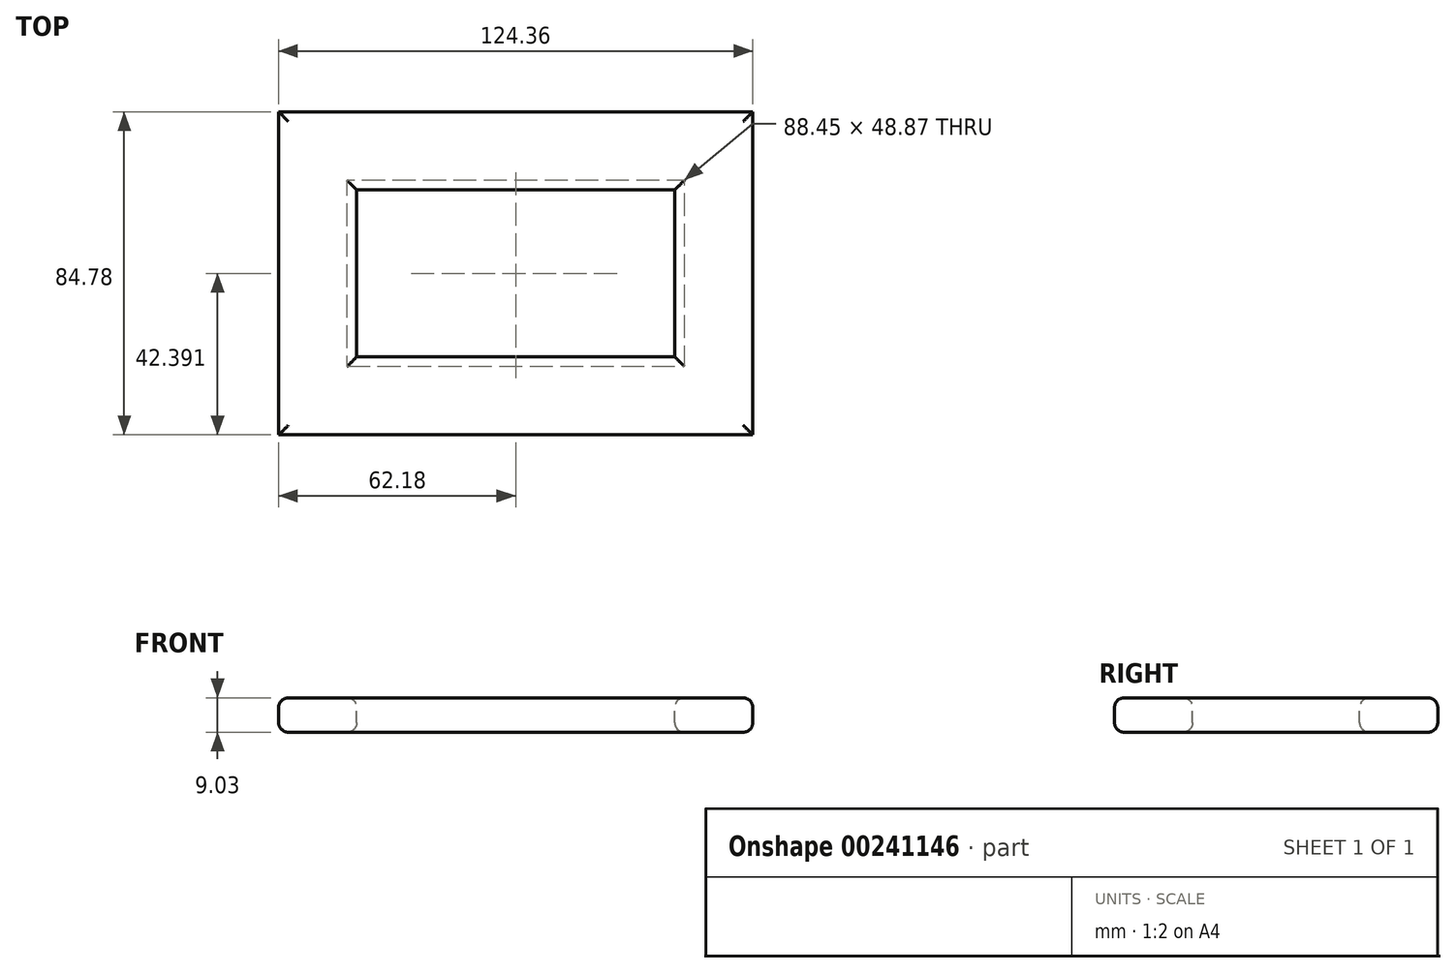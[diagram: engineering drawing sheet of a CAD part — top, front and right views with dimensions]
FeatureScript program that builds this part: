
annotation { "Feature Type Name" : "Feature", "Feature Type Description" : "" }
export const myFeature = defineFeature(function(context is Context, id is Id, definition is map)
    precondition{}
    {
        {
            var Q0;
            Q0=qCreatedBy(makeId("Top.planeOp"),FACE);
            var sketch = newSketch(context, id + "F0", { "sketchPlane" : qUnion([Q0])});
            skLineSegment(sketch, "E0.bottom", {"start": v(-49.05, 27.56) * mm, "end": v(54.15, 27.56) * mm});
            skLineSegment(sketch, "E0.top", {"start": v(-49.05, -36.06) * mm, "end": v(54.15, -36.06) * mm});
            skLineSegment(sketch, "E0.left", {"start": v(-49.05, 27.56) * mm, "end": v(-49.05, -36.06) * mm});
            skLineSegment(sketch, "E0.right", {"start": v(54.15, 27.56) * mm, "end": v(54.15, -36.06) * mm});
            skSolve(sketch);
        }
        {
            var Q0;
            Q0=sQuery(id+"F0.wireOp",VERTEX,"E0.left.end");
            var Q1;
            Q1=sQuery(id+"F0.wireOp",EDGE,"E0.left");
            cPlane(context, id + "F1", {"entities" : qUnion([Q0, Q1]), "cplaneType" : CPlaneType.CURVE_POINT, "offset" : 25.4 * mm, "width" : 152.4 * mm, "height" : 152.4 * mm});
        }
        {
            var Q0;
            Q0=qCreatedBy(id+"F1.planeOp",FACE);
            var sketch = newSketch(context, id + "F2", { "sketchPlane" : qUnion([Q0])});
            skLineSegment(sketch, "E1.bottom", {"start": v(-57.09, 5.01) * mm, "end": v(-41.67, 5.01) * mm});
            skLineSegment(sketch, "E1.top", {"start": v(-57.09, -4.02) * mm, "end": v(-41.67, -4.02) * mm});
            skLineSegment(sketch, "E1.left", {"start": v(-59.63, 2.47) * mm, "end": v(-59.63, -1.48) * mm});
            skLineSegment(sketch, "E1.right", {"start": v(-39.13, 2.47) * mm, "end": v(-39.13, -1.48) * mm});
            skPoint(sketch, "E2.visualSharp", {"position": v(-59.63, 5.01) * mm});
            skArc(sketch, "E2.filletArc", {"start": v(-57.09, 5.01) * mm, "mid": v(-58.88, 4.27) * mm, "end": v(-59.63, 2.47) * mm});
            skPoint(sketch, "E3.visualSharp", {"position": v(-39.13, 5.01) * mm});
            skArc(sketch, "E3.filletArc", {"start": v(-39.13, 2.47) * mm, "mid": v(-39.88, 4.27) * mm, "end": v(-41.67, 5.01) * mm});
            skPoint(sketch, "E4.visualSharp", {"position": v(-39.13, -4.02) * mm});
            skArc(sketch, "E4.filletArc", {"start": v(-41.67, -4.02) * mm, "mid": v(-39.88, -3.27) * mm, "end": v(-39.13, -1.48) * mm});
            skPoint(sketch, "E5.visualSharp", {"position": v(-59.63, -4.02) * mm});
            skArc(sketch, "E5.filletArc", {"start": v(-59.63, -1.48) * mm, "mid": v(-58.88, -3.27) * mm, "end": v(-57.09, -4.02) * mm});
            skSolve(sketch);
        }
        {
            var Q0;
            Q0 = qSketchRegion(id + "F2", true);
            var Q1;
            Q1=sQuery(id+"F0.wireOp",EDGE,"E0.left");
            var Q2;
            Q2=sQuery(id+"F0.wireOp",EDGE,"E0.bottom");
            var Q3;
            Q3=sQuery(id+"F0.wireOp",EDGE,"E0.right");
            var Q4;
            Q4=sQuery(id+"F0.wireOp",EDGE,"E0.top");
            sweep(context, id + "F3", {"profiles" : qUnion([Q0]), "path" : qUnion([Q1, Q2, Q3, Q4])});
        }
    });
